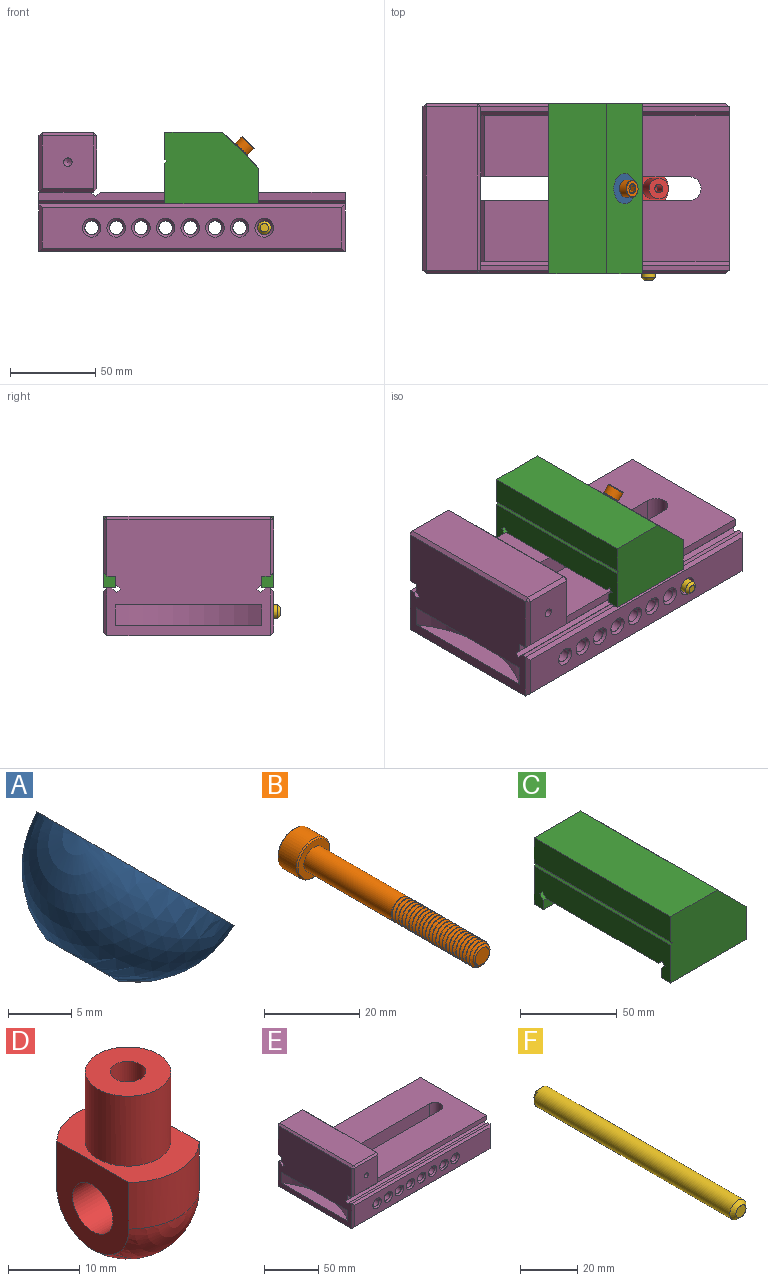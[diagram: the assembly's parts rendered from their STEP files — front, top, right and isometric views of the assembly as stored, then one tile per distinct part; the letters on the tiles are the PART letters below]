
ASSEMBLY  parts=6 mates=5
PART A: 3 faces, bbox 15.4x18x15.4 mm
  f0: sphere r=9mm, area 473.5mm2, adj f1,f2
  f1: plane 18x12.73mm, normal (0.71,0,0.71), area 220.3mm2, adj f0,f2
  f2: cylinder r=3.3mm len=10.59mm, axis (0.71,0,0.71), area 173.6mm2, adj f0,f1
PART B: 49 faces, bbox 11.1x57.3x11.1 mm
  f0: bspline ~24.71x6.93mm, area 299mm2, adj f2,f3,f4,f5,f6,f7,f8,f9
  f1: bspline ~24.38x6.93mm, area 298.1mm2, adj f2,f3,f4,f5,f6,f7,f8,f9
  f2: cylinder r=2.35mm len=23.82mm, axis (0,1,0), area 97.4mm2, adj f0,f1,f27,f30
  f3: cylinder r=3mm len=26.88mm, axis (0,-1,0), area 490mm2, adj f0,f1,f4,f29,f33
  f4: cylinder r=3mm len=6mm, axis (0,-1,0), area 2.4mm2, adj f0,f1,f3,f5
  f5: cylinder r=3mm len=6mm, axis (0,-1,0), area 2.4mm2, adj f0,f1,f4,f6
  f6: cylinder r=3mm len=6mm, axis (0,-1,0), area 2.4mm2, adj f0,f1,f5,f7
  f7: cylinder r=3mm len=6mm, axis (0,-1,0), area 2.4mm2, adj f0,f1,f6,f8
  f8: cylinder r=3mm len=6mm, axis (0,-1,0), area 2.4mm2, adj f0,f1,f7,f9
  f9: cylinder r=3mm len=6mm, axis (0,-1,0), area 2.4mm2, adj f0,f1,f8,f10
  f10: cylinder r=3mm len=6mm, axis (0,-1,0), area 2.4mm2, adj f0,f1,f9,f11
  f11: cylinder r=3mm len=6mm, axis (0,-1,0), area 2.4mm2, adj f0,f1,f10,f12
  f12: cylinder r=3mm len=6mm, axis (0,-1,0), area 2.4mm2, adj f0,f1,f11,f13
  f13: cylinder r=3mm len=6mm, axis (0,-1,0), area 2.4mm2, adj f0,f1,f12,f14
  f14: cylinder r=3mm len=6mm, axis (0,-1,0), area 2.4mm2, adj f0,f1,f13,f15
  f15: cylinder r=3mm len=6mm, axis (0,-1,0), area 2.4mm2, adj f0,f1,f14,f16
  f16: cylinder r=3mm len=6mm, axis (0,-1,0), area 2.4mm2, adj f0,f1,f15,f17
  f17: cylinder r=3mm len=6mm, axis (0,-1,0), area 2.4mm2, adj f0,f1,f16,f18
  f18: cylinder r=3mm len=6mm, axis (0,-1,0), area 2.4mm2, adj f0,f1,f17,f19
  f19: cylinder r=3mm len=6mm, axis (0,-1,0), area 2.4mm2, adj f0,f1,f18,f20
  f20: cylinder r=3mm len=6mm, axis (0,-1,0), area 2.4mm2, adj f0,f1,f19,f21
  f21: cylinder r=3mm len=6mm, axis (0,-1,0), area 2.4mm2, adj f0,f1,f20,f22
  f22: cylinder r=3mm len=6mm, axis (0,-1,0), area 2.4mm2, adj f0,f1,f21,f23
  f23: cylinder r=3mm len=6mm, axis (0,-1,0), area 2.4mm2, adj f0,f1,f22,f24
  f24: cylinder r=3mm len=6mm, axis (0,-1,0), area 2.4mm2, adj f0,f1,f23,f25
  f25: cylinder r=3mm len=6mm, axis (0,-1,0), area 2.4mm2, adj f0,f1,f24,f26
  f26: cylinder r=3mm len=6mm, axis (0,-1,0), area 1.3mm2, adj f0,f1,f25,f27
  f27: cone r=2.1mm half-angle=55deg, axis (0,1,0), area 10.8mm2, adj f0,f1,f2,f26,f28
  f28: plane 4.19x4.19mm, normal (0,-1,0), area 13.8mm2, adj f27
  f29: cone r=3mm half-angle=70deg, axis (0,1,0), area 4.3mm2, adj f0,f1,f3,f30
  f30: plane 5.26x3.76mm, normal (0,-1,0), area 1.6mm2, adj f0,f1,f2,f29
  f31: cylinder r=5mm len=10mm, axis (0,-1,0), area 169.6mm2, adj f47,f48
  f32: plane 10.34x10.34mm, normal (0,1,0), area 43.2mm2, adj f34,f35,f36,f37,f38,f39,f47
  f33: plane 9.4x9.4mm, normal (0,-1,0), area 41.1mm2, adj f3,f48
  f34: cone r=2.89mm half-angle=45deg, axis (0,1,0), area 0mm2, adj f32,f41
  f35: cone r=2.89mm half-angle=45deg, axis (0,1,0), area 0mm2, adj f32,f42
  f36: cone r=2.89mm half-angle=45deg, axis (0,1,0), area 0mm2, adj f32,f43
  f37: cone r=2.89mm half-angle=45deg, axis (0,1,0), area 0mm2, adj f32,f44
  f38: cone r=2.89mm half-angle=45deg, axis (0,1,0), area 0mm2, adj f32,f45
  f39: cone r=2.89mm half-angle=45deg, axis (0,1,0), area 0mm2, adj f32,f46
  f40: plane 5.77x5mm, normal (0,1,0), area 21.7mm2, adj f41,f42,f43,f44,f45,f46
  f41: plane 4.84x3.59mm, normal (-0.5,0,-0.87), area 10.1mm2, adj f34,f40,f42,f46
  f42: plane 4.85x3.99mm, normal (-1,0,0), area 10.1mm2, adj f35,f40,f41,f43
  f43: plane 4.84x3.59mm, normal (-0.5,0,0.87), area 10.1mm2, adj f36,f40,f42,f44
  f44: plane 4.84x3.59mm, normal (0.5,0,0.87), area 10.1mm2, adj f37,f40,f43,f45
  f45: plane 4.85x3.99mm, normal (1,0,0), area 10.1mm2, adj f38,f40,f44,f46
  f46: plane 4.84x3.59mm, normal (0.5,0,-0.87), area 10.1mm2, adj f39,f40,f41,f45
  f47: cone r=4.7mm half-angle=45deg, axis (0,-1,0), area 12.9mm2, adj f31,f32
  f48: cone r=5mm half-angle=45deg, axis (0,1,0), area 12.9mm2, adj f31,f33
PART C: 24 faces, bbox 55x100x46.8 mm
  f0: sphere r=9mm, area 402.8mm2, adj f12,f21
  f1: plane 55x5.88mm, normal (0,1,0), area 323.3mm2, adj f3,f4,f8,f20
  f2: plane 81.76x55mm, normal (0,0,-1), area 4136.8mm2, adj f3,f4,f15,f18,f23
  f3: plane 100x24mm, normal (-1,0,0), area 1692.5mm2, adj f1,f2,f5,f6,f8,f9,f10,f13
  f4: plane 100x21mm, normal (1,0,0), area 1392.5mm2, adj f1,f2,f5,f6,f8,f9,f10,f12
  f5: plane 55x42mm, normal (0,1,0), area 2088.5mm2, adj f3,f4,f7,f10,f11,f12,f13,f14
  f6: plane 55x42mm, normal (0,-1,0), area 2088.5mm2, adj f3,f4,f7,f8,f11,f12,f13,f14
  f7: plane 100x34mm, normal (0,0,1), area 3400mm2, adj f5,f6,f11,f12
  f8: plane 55x7mm, normal (0,0,-1), area 385mm2, adj f1,f3,f4,f6
  f9: plane 55x5.88mm, normal (0,-1,0), area 323.3mm2, adj f3,f4,f10,f16
  f10: plane 55x7mm, normal (0,0,-1), area 385mm2, adj f3,f4,f5,f9
  f11: plane 100x16mm, normal (-1,0,0), area 1600mm2, adj f5,f6,f7,f14
  f12: plane 100x21mm, normal (0.71,0,0.71), area 2715.4mm2, adj f0,f4,f5,f6,f7
  f13: plane 100x1mm, normal (-0.71,0,0.71), area 141.4mm2, adj f3,f5,f6,f14
  f14: plane 100x1mm, normal (-0.71,0,-0.71), area 141.4mm2, adj f5,f6,f11,f13
  f15: plane 55x2.83mm, normal (0,0.71,-0.71), area 220mm2, adj f2,f3,f4,f17
  f16: plane 55x2.83mm, normal (0,-0.71,0.71), area 220mm2, adj f3,f4,f9,f17
  f17: plane 55x2.12mm, normal (0,-0.71,-0.71), area 165mm2, adj f3,f4,f15,f16
  f18: plane 55x2.83mm, normal (0,-0.71,-0.71), area 220mm2, adj f2,f3,f4,f19
  f19: plane 55x2.12mm, normal (0,0.71,-0.71), area 165mm2, adj f3,f4,f18,f20
  f20: plane 55x2.83mm, normal (0,0.71,0.71), area 220mm2, adj f1,f3,f4,f19
  f21: cylinder r=5.5mm len=11mm, axis (0.71,0,0.71), area 133.9mm2, adj f0,f22
  f22: plane 18x12.73mm, normal (-0.71,0,-0.71), area 159.4mm2, adj f21,f23
  f23: cylinder r=9mm len=34.9mm, axis (0.71,0,0.71), area 1257.3mm2, adj f2,f22
PART D: 11 faces, bbox 20x20x30 mm
  f0: cylinder r=10mm len=14mm, axis (0,0,-1), area 124.1mm2, adj f2,f3,f6,f7
  f1: cylinder r=10mm len=14mm, axis (0,0,-1), area 124.1mm2, adj f2,f3,f6,f7
  f2: plane 20x14mm, normal (0,0,1), area 142mm2, adj f0,f1,f4,f6,f7
  f3: sphere r=10mm, area 439.8mm2, adj f0,f1,f6,f7
  f4: cylinder r=6mm len=12mm, axis (0,0,-1), area 452.4mm2, adj f2,f5
  f5: plane 12x12mm, normal (0,0,1), area 93.5mm2, adj f4,f10
  f6: plane 15.14x14.28mm, normal (1,0,0), area 144.1mm2, adj f0,f1,f2,f3,f8
  f7: plane 15.14x14.28mm, normal (-1,0,0), area 144.1mm2, adj f0,f1,f2,f3,f8
  f8: cylinder r=4mm len=14mm, axis (-1,0,0), area 351.9mm2, adj f6,f7
  f9: cone r=0mm half-angle=59deg, axis (0,0,1), area 22.9mm2, adj f10
  f10: cylinder r=2.5mm len=10mm, axis (0,0,1), area 157.1mm2, adj f5,f9
PART E: 96 faces, bbox 180x100x70 mm
  f0: plane 96x68mm, normal (-1,0,0), area 5406.5mm2, adj f1,f2,f15,f26,f27,f28,f29,f30
  f1: plane 180x2.88mm, normal (0,0,1), area 518.2mm2, adj f0,f3,f33,f78
  f2: plane 180x2.88mm, normal (0,0,1), area 518.2mm2, adj f0,f3,f32,f74
  f3: plane 96x35mm, normal (1,0,0), area 2238.5mm2, adj f1,f2,f4,f15,f27,f29,f30,f31
  f4: plane 143.88x86mm, normal (0,0,1), area 10611.3mm2, adj f3,f8,f13,f14,f19,f25,f27,f29
  f5: plane 176x24mm, normal (0,-1,0), area 3463.7mm2, adj f65,f66,f67,f68,f69,f70,f71,f73
  f6: plane 176x24mm, normal (0,1,0), area 3463.7mm2, adj f58,f59,f60,f61,f62,f63,f64,f72
  f7: plane 36x2.12mm, normal (0.71,0,0.71), area 108mm2, adj f8,f9,f14,f29
  f8: plane 36x2.83mm, normal (-0.71,0,0.71), area 144mm2, adj f4,f7,f14,f29
  f9: plane 98.12x2.83mm, normal (0.71,0,-0.71), area 363.2mm2, adj f7,f10,f12,f13,f14,f24,f26,f27
  f10: plane 96x30.88mm, normal (1,0,0), area 2964.4mm2, adj f9,f82,f83,f84
  f11: plane 31x30mm, normal (0,-1,0), area 910.4mm2, adj f21,f82,f86,f89,f90
  f12: plane 15.38x14mm, normal (0,0,-1), area 194.3mm2, adj f9,f13,f14,f18
  f13: plane 133x35mm, normal (0,1,0), area 4245.4mm2, adj f4,f9,f12,f15,f18,f19,f24,f25
  f14: plane 133x35mm, normal (0,-1,0), area 4245.4mm2, adj f4,f7,f8,f9,f12,f15,f18,f19
  f15: plane 180x96mm, normal (0,0,-1), area 15264.1mm2, adj f0,f3,f13,f14,f18,f19,f77,f81
  f16: plane 96x30mm, normal (0,0,1), area 2880mm2, adj f84,f89,f92,f95
  f17: plane 31x30mm, normal (0,1,0), area 910.4mm2, adj f23,f83,f87,f91,f92
  f18: cylinder r=7mm len=35mm, axis (0,0,-1), area 769.7mm2, adj f12,f13,f14,f15
  f19: cylinder r=7mm len=35mm, axis (0,0,-1), area 769.7mm2, adj f4,f13,f14,f15
  f20: cone r=0mm half-angle=59deg, axis (0,-1,0), area 22.9mm2, adj f21
  f21: cylinder r=2.5mm len=13mm, axis (0,-1,0), area 204.2mm2, adj f11,f20
  f22: cone r=0mm half-angle=59deg, axis (0,1,0), area 22.9mm2, adj f23
  f23: cylinder r=2.5mm len=13mm, axis (0,1,0), area 204.2mm2, adj f17,f22
  f24: plane 36x2.12mm, normal (0.71,0,0.71), area 108mm2, adj f9,f13,f25,f27
  f25: plane 36x2.83mm, normal (-0.71,0,0.71), area 144mm2, adj f4,f13,f24,f27
  f26: plane 31.88x5mm, normal (0,0,-1), area 159.4mm2, adj f0,f9,f27,f86
  f27: plane 180x4.88mm, normal (0,-1,0), area 870.7mm2, adj f0,f3,f4,f9,f24,f25,f26,f34
  f28: plane 31.88x5mm, normal (0,0,-1), area 159.4mm2, adj f0,f9,f29,f87
  f29: plane 180x4.88mm, normal (0,1,0), area 870.7mm2, adj f0,f3,f4,f7,f8,f9,f28,f30
  f30: plane 180x2.83mm, normal (0,0.71,-0.71), area 720mm2, adj f0,f3,f29,f31
  f31: plane 180x2.12mm, normal (0,0.71,0.71), area 540mm2, adj f0,f3,f30,f32
  f32: plane 180x2.83mm, normal (0,-0.71,0.71), area 720mm2, adj f0,f2,f3,f31
  f33: plane 180x2.83mm, normal (0,0.71,0.71), area 720mm2, adj f0,f1,f3,f35
  f34: plane 180x2.83mm, normal (0,-0.71,-0.71), area 720mm2, adj f0,f3,f27,f35
  f35: plane 180x2.12mm, normal (0,-0.71,0.71), area 540mm2, adj f0,f3,f33,f34
  f36: cylinder r=75mm len=86mm, axis (0,0,1), area 1099mm2, adj f3,f37,f38
  f37: plane 86x13.55mm, normal (0,0,1), area 792.1mm2, adj f3,f36
  f38: plane 86x13.55mm, normal (0,0,-1), area 792.1mm2, adj f3,f36
  f39: cylinder r=75mm len=86mm, axis (0,0,1), area 1099mm2, adj f0,f40,f41
  f40: plane 86x13.55mm, normal (0,0,1), area 792.1mm2, adj f0,f39
  f41: plane 86x13.55mm, normal (0,0,-1), area 792.1mm2, adj f0,f39
  f42: cylinder r=4mm len=41.5mm, axis (0,-1,0), area 1043mm2, adj f14,f72
  f43: cylinder r=4mm len=41.5mm, axis (0,-1,0), area 1043mm2, adj f13,f73
  f44: cylinder r=4mm len=41.5mm, axis (0,-1,0), area 1043mm2, adj f14,f64
  f45: cylinder r=4mm len=41.5mm, axis (0,-1,0), area 1043mm2, adj f13,f71
  f46: cylinder r=4mm len=41.5mm, axis (0,-1,0), area 1043mm2, adj f14,f63
  f47: cylinder r=4mm len=41.5mm, axis (0,-1,0), area 1043mm2, adj f13,f70
  f48: cylinder r=4mm len=41.5mm, axis (0,-1,0), area 1043mm2, adj f14,f62
  f49: cylinder r=4mm len=41.5mm, axis (0,-1,0), area 1043mm2, adj f13,f69
  f50: cylinder r=4mm len=41.5mm, axis (0,-1,0), area 1043mm2, adj f14,f61
  f51: cylinder r=4mm len=41.5mm, axis (0,-1,0), area 1043mm2, adj f13,f68
  f52: cylinder r=4mm len=41.5mm, axis (0,-1,0), area 1043mm2, adj f14,f60
  f53: cylinder r=4mm len=41.5mm, axis (0,-1,0), area 1043mm2, adj f13,f67
  f54: cylinder r=4mm len=41.5mm, axis (0,-1,0), area 1043mm2, adj f14,f59
  f55: cylinder r=4mm len=41.5mm, axis (0,-1,0), area 1043mm2, adj f13,f66
  f56: cylinder r=4mm len=41.5mm, axis (0,-1,0), area 1043mm2, adj f14,f58
  f57: cylinder r=4mm len=41.5mm, axis (0,-1,0), area 1043mm2, adj f13,f65
  f58: cone r=4mm half-angle=45deg, axis (0,1,0), area 63.3mm2, adj f6,f56
  f59: cone r=4mm half-angle=45deg, axis (0,1,0), area 63.3mm2, adj f6,f54
  f60: cone r=4mm half-angle=45deg, axis (0,1,0), area 63.3mm2, adj f6,f52
  f61: cone r=4mm half-angle=45deg, axis (0,1,0), area 63.3mm2, adj f6,f50
  f62: cone r=4mm half-angle=45deg, axis (0,1,0), area 63.3mm2, adj f6,f48
  f63: cone r=4mm half-angle=45deg, axis (0,1,0), area 63.3mm2, adj f6,f46
  f64: cone r=4mm half-angle=45deg, axis (0,1,0), area 63.3mm2, adj f6,f44
  f65: cone r=4mm half-angle=45deg, axis (0,-1,0), area 63.3mm2, adj f5,f57
  f66: cone r=4mm half-angle=45deg, axis (0,-1,0), area 63.3mm2, adj f5,f55
  f67: cone r=4mm half-angle=45deg, axis (0,-1,0), area 63.3mm2, adj f5,f53
  f68: cone r=4mm half-angle=45deg, axis (0,-1,0), area 63.3mm2, adj f5,f51
  f69: cone r=4mm half-angle=45deg, axis (0,-1,0), area 63.3mm2, adj f5,f49
  f70: cone r=4mm half-angle=45deg, axis (0,-1,0), area 63.3mm2, adj f5,f47
  f71: cone r=4mm half-angle=45deg, axis (0,-1,0), area 63.3mm2, adj f5,f45
  f72: cone r=4mm half-angle=45deg, axis (0,1,0), area 63.3mm2, adj f6,f42
  f73: cone r=4mm half-angle=45deg, axis (0,-1,0), area 63.3mm2, adj f5,f43
  f74: plane 180x2mm, normal (0,0.71,0.71), area 503.5mm2, adj f2,f6,f75,f76
  f75: plane 28x2mm, normal (-0.71,0.71,0), area 73.5mm2, adj f0,f6,f74,f77
  f76: plane 28x2mm, normal (0.71,0.71,0), area 73.5mm2, adj f3,f6,f74,f77
  f77: plane 180x2mm, normal (0,0.71,-0.71), area 503.5mm2, adj f6,f15,f75,f76
  f78: plane 180x2mm, normal (0,-0.71,0.71), area 503.5mm2, adj f1,f5,f79,f80
  f79: plane 28x2mm, normal (-0.71,-0.71,0), area 73.5mm2, adj f0,f5,f78,f81
  f80: plane 28x2mm, normal (0.71,-0.71,0), area 73.5mm2, adj f3,f5,f78,f81
  f81: plane 180x2mm, normal (0,-0.71,-0.71), area 503.5mm2, adj f5,f15,f79,f80
  f82: plane 31.94x2mm, normal (0.71,-0.71,0), area 88.9mm2, adj f9,f10,f11,f85,f86
  f83: plane 31.94x2mm, normal (0.71,0.71,0), area 88.9mm2, adj f9,f10,f17,f87,f88
  f84: plane 96x2mm, normal (0.71,0,0.71), area 271.5mm2, adj f10,f16,f85,f88
  f85: plane 2x2mm, normal (0.58,-0.58,0.58), area 3.5mm2, adj f82,f84,f89
  f86: plane 32.94x2mm, normal (0,-0.71,-0.71), area 88.9mm2, adj f9,f11,f26,f82,f90
  f87: plane 32.94x2mm, normal (0,0.71,-0.71), area 88.9mm2, adj f9,f17,f28,f83,f91
  f88: plane 2x2mm, normal (0.58,0.58,0.58), area 3.5mm2, adj f83,f84,f92
  f89: plane 30x2mm, normal (0,-0.71,0.71), area 84.9mm2, adj f11,f16,f85,f93
  f90: plane 33x2mm, normal (-0.71,-0.71,0), area 90.5mm2, adj f0,f11,f86,f93
  f91: plane 33x2mm, normal (-0.71,0.71,0), area 90.5mm2, adj f0,f17,f87,f94
  f92: plane 30x2mm, normal (0,0.71,0.71), area 84.9mm2, adj f16,f17,f88,f94
  f93: plane 2x2mm, normal (-0.58,-0.58,0.58), area 3.5mm2, adj f89,f90,f95
  f94: plane 2x2mm, normal (-0.58,0.58,0.58), area 3.5mm2, adj f91,f92,f95
  f95: plane 96x2mm, normal (-0.71,0,0.71), area 271.5mm2, adj f0,f16,f93,f94
PART F: 5 faces, bbox 8x100x8 mm
  f0: plane 5x5mm, normal (0,1,0), area 19.6mm2, adj f3
  f1: cylinder r=4mm len=97mm, axis (0,-1,0), area 2437.9mm2, adj f3,f4
  f2: plane 5x5mm, normal (0,-1,0), area 19.6mm2, adj f4
  f3: cone r=2.5mm half-angle=45deg, axis (0,-1,0), area 43.3mm2, adj f0,f1
  f4: cone r=2.5mm half-angle=45deg, axis (0,1,0), area 43.3mm2, adj f1,f2
PLACE A t=(-74.64,45.69,-23.79)mm
PLACE B rot(axis=(0.86,0.36,-0.36),98.4deg) t=(59.86,45.69,0.72)mm
PLACE C t=(-74.64,45.69,-23.79)mm
PLACE D rot(axis=(0.16,0.16,0.98),91.4deg) t=(108.79,45.75,-9.79)mm
PLACE E t=(-23.71,45.75,-23.79)mm fixed
PLACE F rot(axis=(0,1,0),56.4deg) t=(23.76,41.77,92.79)mm
MATE fastened C.f21 <-> A.f2  axis (0.71,0,0.71) through (94.86,45.69,35.71)mm
MATE planar E.f1 <-> C.f8  axis (0,0,1) through (156.29,-0.81,4.21)mm
MATE slider A.f2 <-> B.f2  axis (0.71,0,0.71) through (94.86,45.69,35.71)mm
MATE cylindrical E.f56 <-> F.f1  axis (0,-1,0) through (108.79,-2.75,-9.79)mm
MATE planar E.f56 <-> D.f8  axis (0,-1,0) through (108.79,52.75,-9.79)mm
